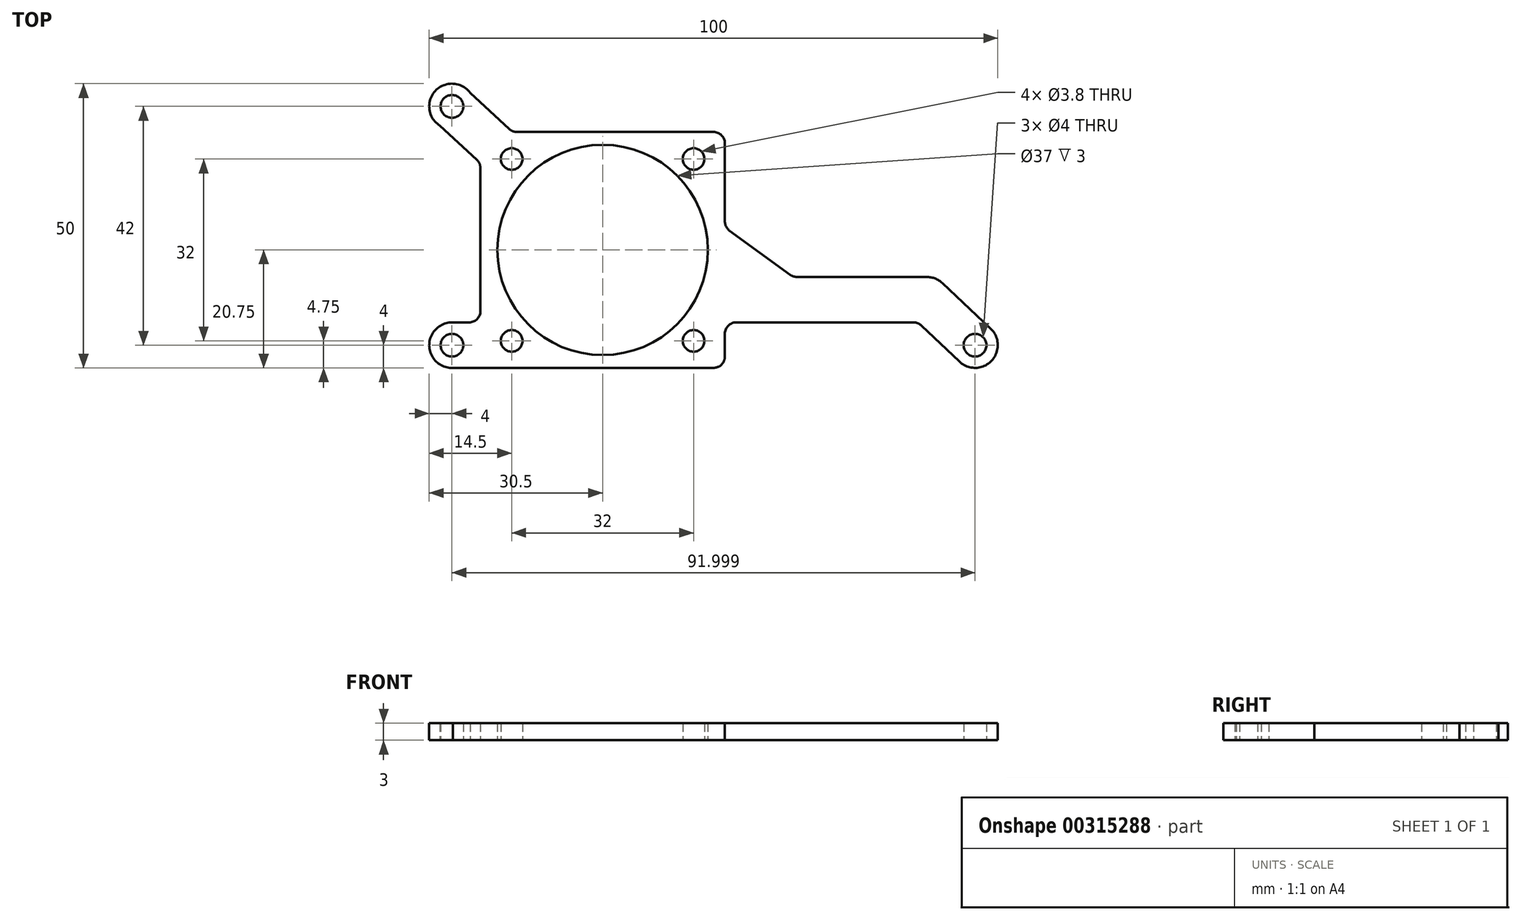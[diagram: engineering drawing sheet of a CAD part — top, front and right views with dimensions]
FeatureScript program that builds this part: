
annotation { "Feature Type Name" : "Feature", "Feature Type Description" : "" }
export const myFeature = defineFeature(function(context is Context, id is Id, definition is map)
    precondition{}
    {
        {
            var Q0;
            Q0=qCreatedBy(makeId("Top.planeOp"),FACE);
            var sketch = newSketch(context, id + "F0", { "sketchPlane" : qUnion([Q0])});
            skPoint(sketch, "E0.middle", {"position": v(0, 0) * mm});
            skCircle(sketch, "E1", {"center": v(-46, 21) * mm, "radius": 2 * mm});
            skCircle(sketch, "E2.MirrorC", {"center": v(-46, -21) * mm, "radius": 2 * mm});
            skCircle(sketch, "E3.MirrorC", {"center": v(46, -21) * mm, "radius": 2 * mm});
            skLineSegment(sketch, "E4.bottom", {"start": v(-35.36, 16.5) * mm, "end": v(2, 16.5) * mm});
            skLineSegment(sketch, "E4.left", {"start": v(-41, 11.05) * mm, "end": v(-41, -17) * mm});
            skLineSegment(sketch, "E5", {"start": v(14, -17) * mm, "end": v(2, -17) * mm});
            skLineSegment(sketch, "E6", {"start": v(2, -17) * mm, "end": v(2, -25) * mm});
            skPoint(sketch, "E7.middle", {"position": v(-19.5, -4.25) * mm});
            skCircle(sketch, "E8", {"center": v(-35.5, 11.75) * mm, "radius": 1.9 * mm});
            skCircle(sketch, "E9", {"center": v(-19.5, -4.25) * mm, "radius": 18.5 * mm});
            skArc(sketch, "E10", {"start": v(-42.78, 23.38) * mm, "mid": v(-48.94, 23.71) * mm, "end": v(-48.11, 17.6) * mm});
            skArc(sketch, "E11.MirrorC", {"start": v(-45.87, -25) * mm, "mid": v(-50, -21.07) * mm, "end": v(-46, -17) * mm});
            skArc(sketch, "E12.MirrorC", {"start": v(43.24, -23.9) * mm, "mid": v(48.9, -23.75) * mm, "end": v(48.74, -18.09) * mm});
            skPoint(sketch, "E13.orphan", {"position": v(14, -25) * mm});
            skLineSegment(sketch, "E14", {"start": v(-46, -17) * mm, "end": v(-41, -17) * mm});
            skLineSegment(sketch, "E15", {"start": v(-48.11, 17.6) * mm, "end": v(-41, 11.05) * mm});
            skLineSegment(sketch, "E16", {"start": v(-42.78, 23.38) * mm, "end": v(-35.36, 16.5) * mm});
            skLineSegment(sketch, "E17.bottom", {"start": v(14, -17) * mm, "end": v(36, -17) * mm});
            skLineSegment(sketch, "E18", {"start": v(36, -17) * mm, "end": v(43.24, -23.9) * mm});
            skPoint(sketch, "E19.orphan", {"position": v(-41, 16.5) * mm});
            skPoint(sketch, "E7.bottom.end.orphan", {"position": v(-39.5, 15.75) * mm});
            skPoint(sketch, "E7.left.start.orphan", {"position": v(0.5, 15.75) * mm});
            skPoint(sketch, "E7.top.end.orphan", {"position": v(-39.5, -24.25) * mm});
            skPoint(sketch, "E7.top.start.orphan", {"position": v(0.5, -24.25) * mm});
            skLineSegment(sketch, "E20", {"start": v(39.09, -9) * mm, "end": v(48.74, -18.09) * mm});
            skLineSegment(sketch, "E21", {"start": v(2, -0.25) * mm, "end": v(2, 16.5) * mm});
            skLineSegment(sketch, "E22", {"start": v(14, -9) * mm, "end": v(2, -0.25) * mm});
            skPoint(sketch, "E4.right.start.orphan", {"position": v(14, 16.5) * mm});
            skCircle(sketch, "E23.MirrorC", {"center": v(-3.5, 11.75) * mm, "radius": 1.9 * mm});
            skCircle(sketch, "E24.MirrorC", {"center": v(-35.5, -20.25) * mm, "radius": 1.9 * mm});
            skCircle(sketch, "E25.MirrorC", {"center": v(-3.5, -20.25) * mm, "radius": 1.9 * mm});
            skLineSegment(sketch, "E26", {"start": v(-45.87, -25) * mm, "end": v(2, -25) * mm});
            skLineSegment(sketch, "E27", {"start": v(39.09, -9) * mm, "end": v(14, -9) * mm});
            skSolve(sketch);
        }
        {
            var Q0;
            Q0=makeQuery(id+"F0.imprint","IMPRINT",FACE,{"disambiguationData":[TD([[makeQuery(id+"F0.imprint","IMPRINT",EDGE,{"derivedFrom":sQuery(id+"F0.wireOp",EDGE,"E1")}),-1.0]])]});
            extrude(context, id + "F1", {"entities" : qUnion([Q0]), "depth" : 3 * mm});
        }
        {
            var Q0;
            Q0=makeQuery(id+"F1.opExtrude","SWEPT_EDGE",EDGE,{"disambiguationData":[OSD([sQuery(id+"F0.wireOp",EDGE,"E4.left"),sQuery(id+"F0.wireOp",EDGE,"E14")])]});
            var Q1;
            Q1=makeQuery(id+"F1.opExtrude","SWEPT_EDGE",EDGE,{"disambiguationData":[OSD([sQuery(id+"F0.wireOp",EDGE,"E4.left"),sQuery(id+"F0.wireOp",EDGE,"E15")])]});
            var Q2;
            Q2=makeQuery(id+"F1.opExtrude","SWEPT_EDGE",EDGE,{"disambiguationData":[OSD([sQuery(id+"F0.wireOp",EDGE,"E4.bottom"),sQuery(id+"F0.wireOp",EDGE,"E16")])]});
            var Q3;
            Q3=makeQuery(id+"F1.opExtrude","SWEPT_EDGE",EDGE,{"disambiguationData":[OSD([sQuery(id+"F0.wireOp",EDGE,"E4.bottom"),sQuery(id+"F0.wireOp",EDGE,"E21")])]});
            var Q4;
            Q4=makeQuery(id+"F1.opExtrude","SWEPT_EDGE",EDGE,{"disambiguationData":[OSD([sQuery(id+"F0.wireOp",EDGE,"E4.top"),sQuery(id+"F0.wireOp",EDGE,"E6")])]});
            var Q5;
            Q5=makeQuery(id+"F1.opExtrude","SWEPT_EDGE",EDGE,{"disambiguationData":[OSD([sQuery(id+"F0.wireOp",EDGE,"E5"),sQuery(id+"F0.wireOp",EDGE,"E6")])]});
            var Q6;
            Q6=makeQuery(id+"F1.opExtrude","SWEPT_EDGE",EDGE,{"disambiguationData":[OSD([sQuery(id+"F0.wireOp",EDGE,"E21"),sQuery(id+"F0.wireOp",EDGE,"E22")])]});
            var Q7;
            Q7=makeQuery(id+"F1.opExtrude","SWEPT_EDGE",EDGE,{"disambiguationData":[OSD([sQuery(id+"F0.wireOp",EDGE,"E17.top"),sQuery(id+"F0.wireOp",EDGE,"E22")])]});
            var Q8;
            Q8=makeQuery(id+"F1.opExtrude","SWEPT_EDGE",EDGE,{"disambiguationData":[OSD([sQuery(id+"F0.wireOp",EDGE,"E17.bottom"),sQuery(id+"F0.wireOp",EDGE,"E18")])]});
            fillet(context, id + "F2", {"entities" : qUnion([Q0, Q1, Q2, Q3, Q4, Q5, Q6, Q7, Q8]), "radius" : 2 * mm, "tangentPropagation" : true, "allowEdgeOverflow" : false});
        }
        {
            var Q0;
            Q0=makeQuery(id+"F1.opExtrude","SWEPT_EDGE",EDGE,{"disambiguationData":[OSD([sQuery(id+"F0.wireOp",EDGE,"eTp8448j-vD2S-qsJ5-2Ota-6kCuHiR2TWy8"),sQuery(id+"F0.wireOp",EDGE,"E20")])]});
            fillet(context, id + "F3", {"entities" : qUnion([Q0]), "radius" : 4 * mm, "tangentPropagation" : true, "allowEdgeOverflow" : false});
        }
    });
